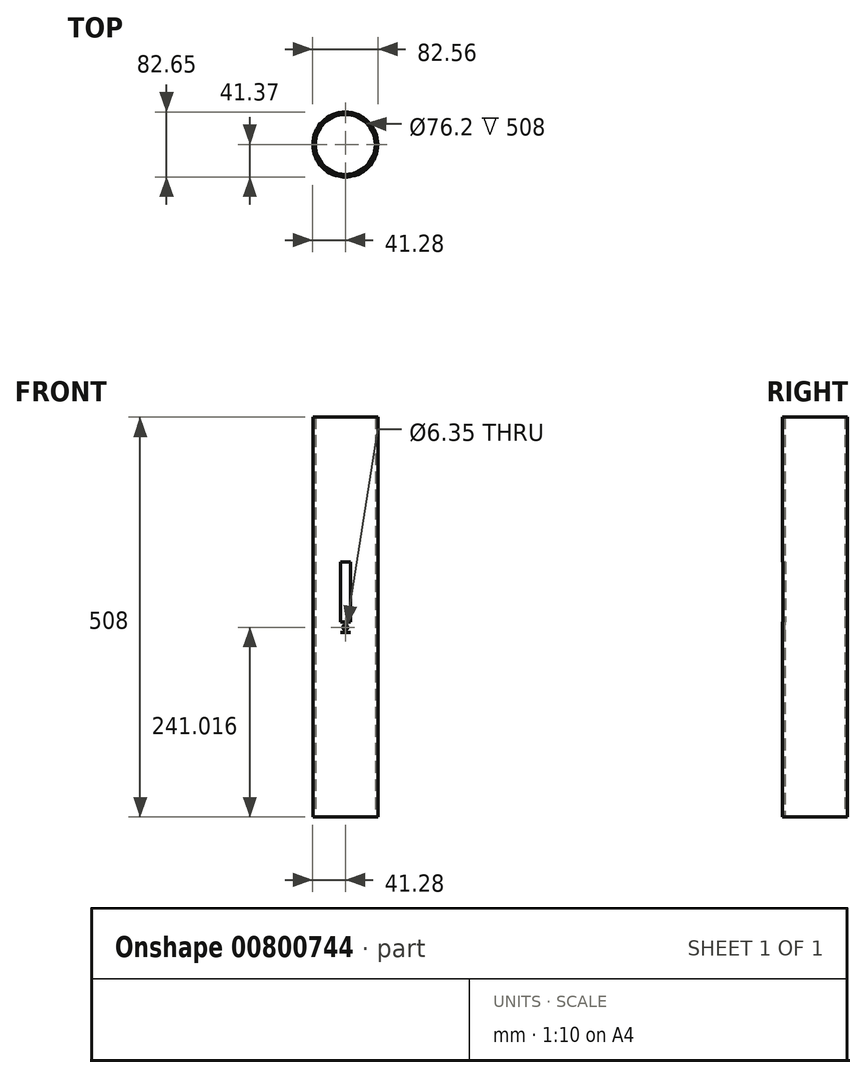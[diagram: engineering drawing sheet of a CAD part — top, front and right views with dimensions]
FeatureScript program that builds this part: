
annotation { "Feature Type Name" : "Feature", "Feature Type Description" : "" }
export const myFeature = defineFeature(function(context is Context, id is Id, definition is map)
    precondition{}
    {
        {
            var Q0;
            Q0=qCreatedBy(makeId("Top.planeOp"),FACE);
            var sketch = newSketch(context, id + "F0", { "sketchPlane" : qUnion([Q0])});
            skCircle(sketch, "E0", {"center": v(0, 0) * mm, "radius": 38.1 * mm});
            skCircle(sketch, "E1", {"center": v(0, 0) * mm, "radius": 41.28 * mm});
            skSolve(sketch);
        }
        {
            var Q0;
            Q0=makeQuery(id+"F0.imprint","IMPRINT",FACE,{"disambiguationData":[TD([[makeQuery(id+"F0.imprint","IMPRINT",EDGE,{"derivedFrom":sQuery(id+"F0.wireOp",EDGE,"E0")}),-1.0]])]});
            extrude(context, id + "F1", {"entities" : qUnion([Q0]), "depth" : 508 * mm, "offsetDistance" : 25.4 * mm});
        }
        {
            var Q0;
            Q0=makeQuery(id+"F1.opExtrude","SWEPT_FACE",FACE,{"disambiguationData":[OSD([sQuery(id+"F0.wireOp",EDGE,"E1")])]});
            cPlane(context, id + "F2", {"entities" : qUnion([Q0]), "cplaneType" : CPlaneType.LINE_ANGLE, "offset" : 25.4 * mm, "angle" : 0 * degree, "width" : 152.4 * mm, "height" : 152.4 * mm});
        }
        {
            var Q0;
            Q0=qCreatedBy(id+"F2.planeOp",FACE);
            var sketch = newSketch(context, id + "F3", { "sketchPlane" : qUnion([Q0])});
            skLineSegment(sketch, "E2.bottom", {"start": v(63.45, 323.78) * mm, "end": v(25.35, 323.78) * mm});
            skLineSegment(sketch, "E2.top", {"start": v(63.45, 247.58) * mm, "end": v(25.35, 247.58) * mm});
            skLineSegment(sketch, "E2.left", {"start": v(63.45, 323.78) * mm, "end": v(63.45, 247.58) * mm});
            skLineSegment(sketch, "E2.right", {"start": v(25.35, 323.78) * mm, "end": v(25.35, 247.58) * mm});
            skLineSegment(sketch, "E3.bottom", {"start": v(41.4, 247.58) * mm, "end": v(39.84, 247.58) * mm});
            skLineSegment(sketch, "E3.top", {"start": v(41.4, 234.28) * mm, "end": v(39.84, 234.28) * mm});
            skLineSegment(sketch, "E3.left", {"start": v(41.4, 247.58) * mm, "end": v(41.4, 234.28) * mm});
            skLineSegment(sketch, "E3.right", {"start": v(39.84, 247.58) * mm, "end": v(39.84, 234.28) * mm});
            skSolve(sketch);
        }
        {
            var Q0;
            Q0=makeQuery(id+"F3.imprint","IMPRINT",FACE,{"disambiguationData":[TD([[makeQuery(id+"F3.imprint","IMPRINT",EDGE,{"derivedFrom":sQuery(id+"F3.wireOp",EDGE,"E2.bottom")}),1.0]])]});
            var Q1;
            {Q1=qUnion([makeQuery(id+"F3.imprint","IMPRINT",FACE,{"disambiguationData":[TD([[makeQuery(id+"F3.imprint","IMPRINT",EDGE,{"derivedFrom":sQuery(id+"F3.wireOp",EDGE,"E2.bottom")}),1.0]])]}),makeQuery(id+"F3.imprint","IMPRINT",FACE,{"disambiguationData":[TD([[makeQuery(id+"F3.imprint","IMPRINT",EDGE,{"derivedFrom":sQuery(id+"F3.wireOp",EDGE,"E3.top")}),-1.0]])]})]);}
            extrude(context, id + "F4", {"entities" : qUnion([Q0, Q1]), "operationType" : NewBodyOperationType.REMOVE, "endBound" : BoundingType.SYMMETRIC, "depth" : 12.7 * mm, "offsetDistance" : 25.4 * mm});
        }
        {
            var Q0;
            Q0=makeQuery(id+"F3.imprint","IMPRINT",FACE,{"disambiguationData":[TD([[makeQuery(id+"F3.imprint","IMPRINT",EDGE,{"derivedFrom":sQuery(id+"F3.wireOp",EDGE,"E3.top")}),-1.0]])]});
            extrude(context, id + "F5", {"entities" : qUnion([Q0]), "operationType" : NewBodyOperationType.ADD, "endBound" : BoundingType.SYMMETRIC, "depth" : 12.7 * mm, "offsetDistance" : 25.4 * mm});
        }
        {
            var Q0;
            Q0=makeQuery(id+"F5.opExtrude","SWEPT_FACE",FACE,{"disambiguationData":[OSD([sQuery(id+"F3.wireOp",EDGE,"E3.left")])]});
            var sketch = newSketch(context, id + "F6", { "sketchPlane" : qUnion([Q0])});
            skCircle(sketch, "E4", {"center": v(0, 241.02) * mm, "radius": 3.18 * mm});
            skSolve(sketch);
        }
        {
            var Q0;
            Q0=makeQuery(id+"F6.imprint","IMPRINT",FACE,{"disambiguationData":[TD([[makeQuery(id+"F6.imprint","IMPRINT",EDGE,{"derivedFrom":sQuery(id+"F6.wireOp",EDGE,"E4")}),1.0]])]});
            extrude(context, id + "F7", {"entities" : qUnion([Q0]), "operationType" : NewBodyOperationType.REMOVE, "oppositeDirection" : true, "depth" : 25.4 * mm, "offsetDistance" : 25.4 * mm});
        }
        {
            var Q0;
            Q0=makeQuery(id+"F5.opExtrude","CAP_EDGE",EDGE,{"disambiguationData":[OSD([sQuery(id+"F3.wireOp",EDGE,"E3.left")])],"isStart":false});
            var Q1;
            Q1=makeQuery(id+"F5.opExtrude","CAP_EDGE",EDGE,{"disambiguationData":[OSD([sQuery(id+"F3.wireOp",EDGE,"E3.left")])],"isStart":true});
            fillet(context, id + "F8", {"entities" : qUnion([Q0, Q1]), "radius" : 50.8 * mm, "tangentPropagation" : true, "allowEdgeOverflow" : false});
        }
    });
